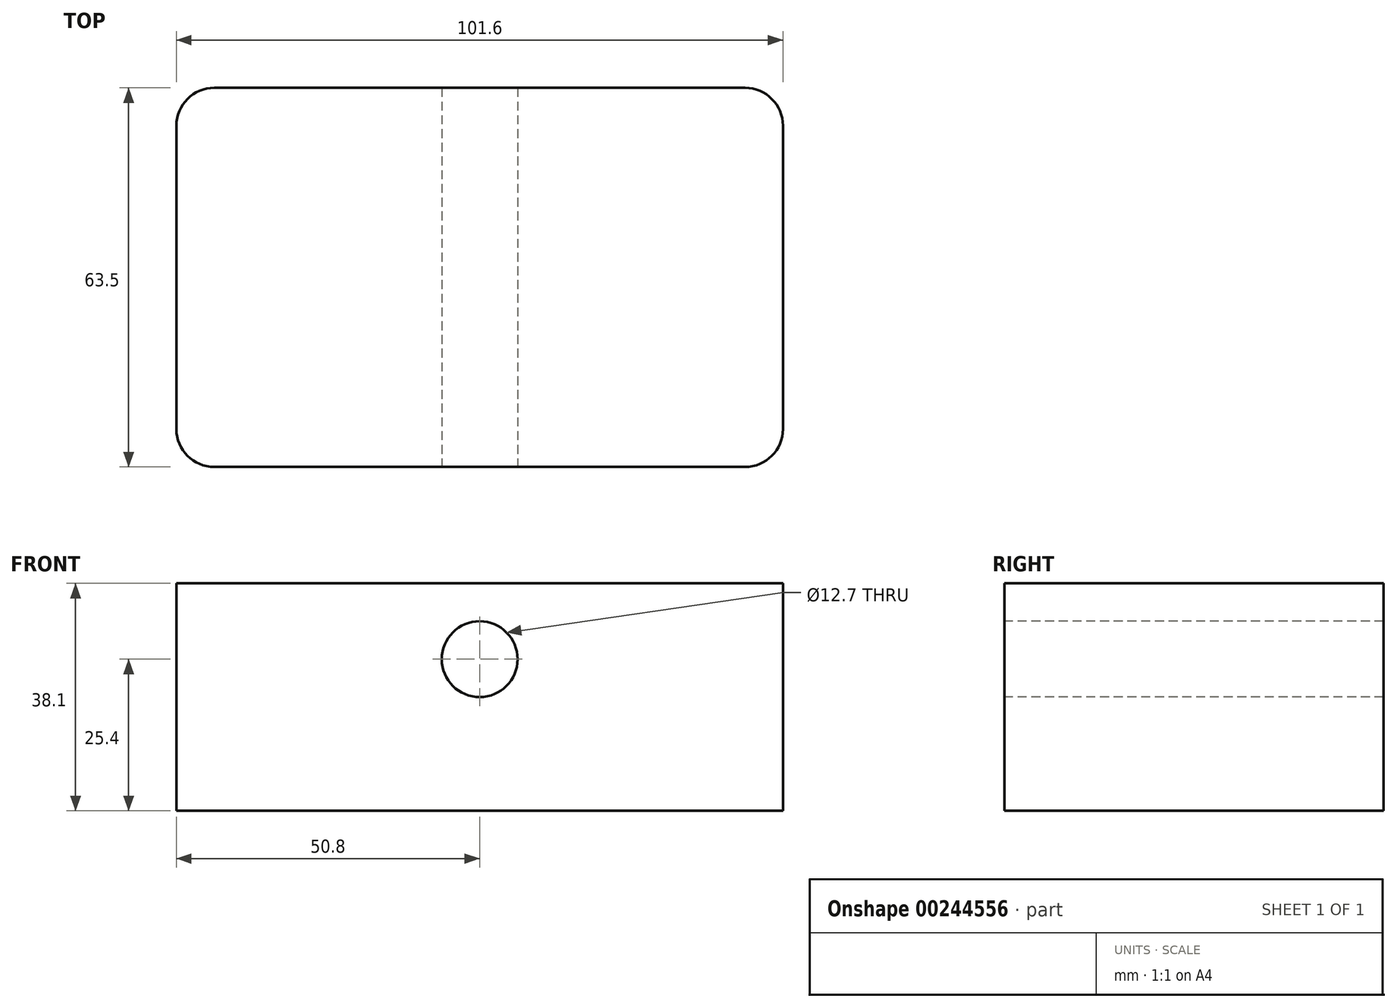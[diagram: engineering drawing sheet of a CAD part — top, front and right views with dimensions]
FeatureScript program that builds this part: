
annotation { "Feature Type Name" : "Feature", "Feature Type Description" : "" }
export const myFeature = defineFeature(function(context is Context, id is Id, definition is map)
    precondition{}
    {
        {
            var Q0;
            Q0=qCreatedBy(makeId("Top.planeOp"),FACE);
            var sketch = newSketch(context, id + "F0", { "sketchPlane" : qUnion([Q0])});
            skLineSegment(sketch, "E0.bottom", {"start": v(6.35, 0) * mm, "end": v(95.25, 0) * mm});
            skLineSegment(sketch, "E0.top", {"start": v(6.35, 63.5) * mm, "end": v(95.25, 63.5) * mm});
            skLineSegment(sketch, "E0.left", {"start": v(0, 6.35) * mm, "end": v(0, 57.15) * mm});
            skLineSegment(sketch, "E0.right", {"start": v(101.6, 6.35) * mm, "end": v(101.6, 57.15) * mm});
            skPoint(sketch, "E1.visualSharp", {"position": v(0, 63.5) * mm});
            skArc(sketch, "E1.filletArc", {"start": v(6.35, 63.5) * mm, "mid": v(1.86, 61.64) * mm, "end": v(0, 57.15) * mm});
            skPoint(sketch, "E2.visualSharp", {"position": v(0, 0) * mm});
            skArc(sketch, "E2.filletArc", {"start": v(0, 6.35) * mm, "mid": v(1.86, 1.86) * mm, "end": v(6.35, 0) * mm});
            skPoint(sketch, "E3.visualSharp", {"position": v(101.6, 0) * mm});
            skArc(sketch, "E3.filletArc", {"start": v(95.25, 0) * mm, "mid": v(99.74, 1.86) * mm, "end": v(101.6, 6.35) * mm});
            skPoint(sketch, "E4.visualSharp", {"position": v(101.6, 63.5) * mm});
            skArc(sketch, "E4.filletArc", {"start": v(101.6, 57.15) * mm, "mid": v(99.74, 61.64) * mm, "end": v(95.25, 63.5) * mm});
            skSolve(sketch);
        }
        {
            var Q0;
            Q0=makeQuery(id+"F0.imprint","IMPRINT",FACE,{"disambiguationData":[TD([[makeQuery(id+"F0.imprint","IMPRINT",EDGE,{"derivedFrom":sQuery(id+"F0.wireOp",EDGE,"E0.bottom")}),1.0]])]});
            extrude(context, id + "F1", {"entities" : qUnion([Q0]), "depth" : 38.1 * mm});
        }
        {
            var Q0;
            Q0=makeQuery(id+"F1.opExtrude","SWEPT_FACE",FACE,{"disambiguationData":[OSD([sQuery(id+"F0.wireOp",EDGE,"E0.bottom")])]});
            var sketch = newSketch(context, id + "F2", { "sketchPlane" : qUnion([Q0])});
            skCircle(sketch, "E5", {"center": v(50.8, 25.4) * mm, "radius": 6.35 * mm});
            skSolve(sketch);
        }
        {
            var Q0;
            Q0=makeQuery(id+"F2.imprint","IMPRINT",FACE,{"disambiguationData":[TD([[makeQuery(id+"F2.imprint","IMPRINT",EDGE,{"derivedFrom":sQuery(id+"F2.wireOp",EDGE,"E5")}),1.0]])]});
            extrude(context, id + "F3", {"entities" : qUnion([Q0]), "operationType" : NewBodyOperationType.REMOVE, "endBound" : BoundingType.THROUGH_ALL, "oppositeDirection" : true, "depth" : 25.4 * mm});
        }
    });
